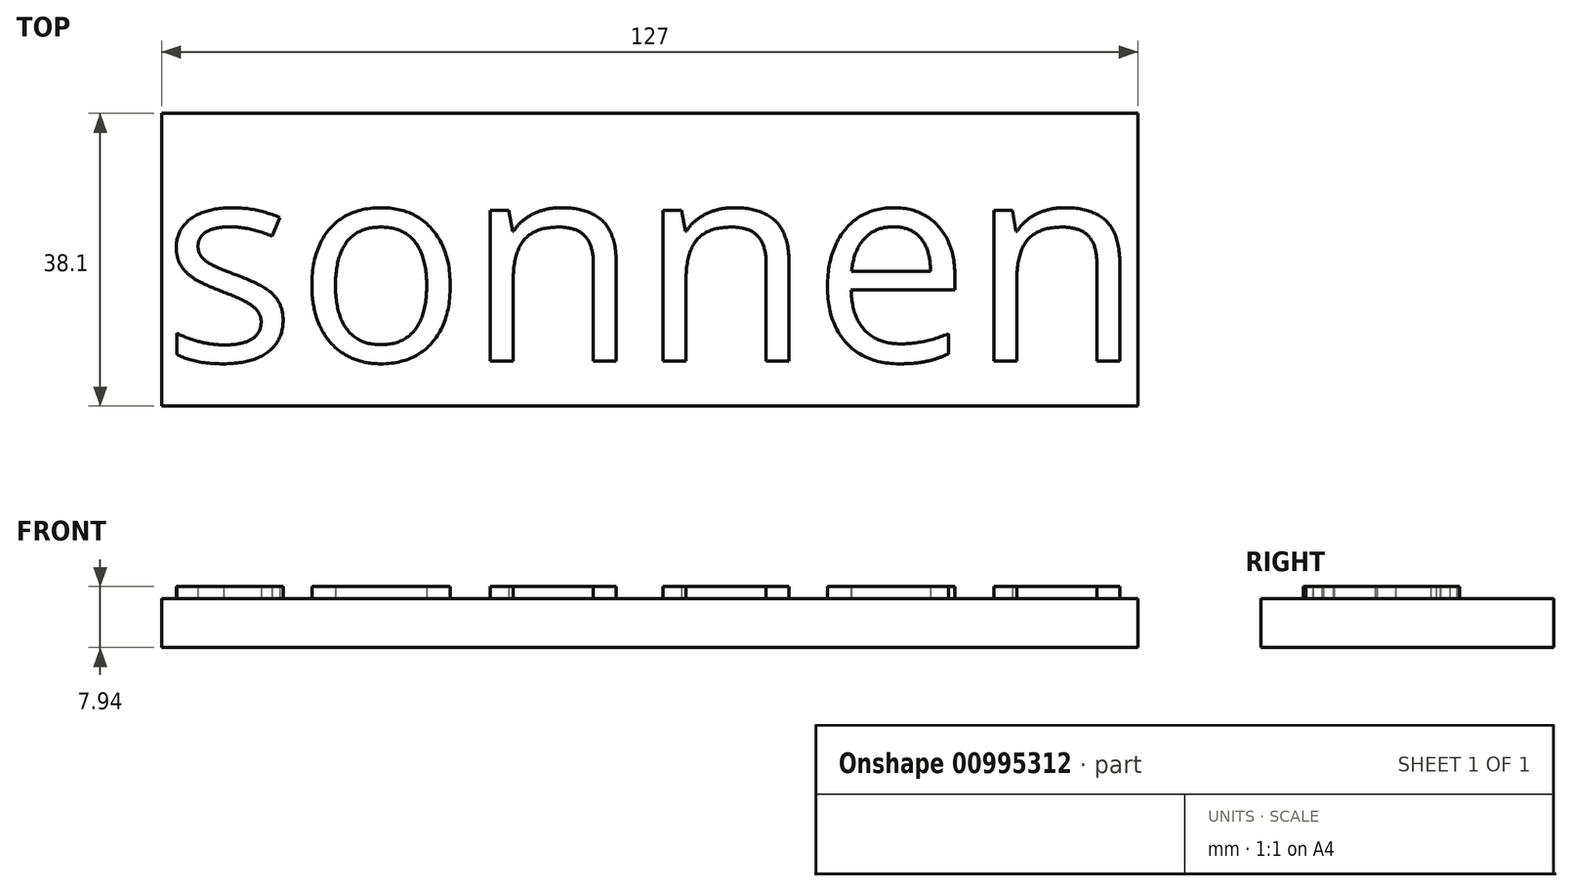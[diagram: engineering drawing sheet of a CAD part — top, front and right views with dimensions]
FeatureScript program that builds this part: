
annotation { "Feature Type Name" : "Feature", "Feature Type Description" : "" }
export const myFeature = defineFeature(function(context is Context, id is Id, definition is map)
    precondition{}
    {
        {
            var Q0;
            Q0=qCreatedBy(makeId("Top.planeOp"),FACE);
            var sketch = newSketch(context, id + "F0", { "sketchPlane" : qUnion([Q0])});
            skLineSegment(sketch, "E0.bottom", {"start": v(-63.5, -19.05) * mm, "end": v(63.5, -19.05) * mm});
            skLineSegment(sketch, "E0.top", {"start": v(-63.5, 19.05) * mm, "end": v(63.5, 19.05) * mm});
            skLineSegment(sketch, "E0.left", {"start": v(-63.5, -19.05) * mm, "end": v(-63.5, 19.05) * mm});
            skLineSegment(sketch, "E0.right", {"start": v(63.5, -19.05) * mm, "end": v(63.5, 19.05) * mm});
            skLineSegment(sketch, "E1", {"start": v(0, 19.05) * mm, "end": v(0, -19.05) * mm, "construction": true});
            skLineSegment(sketch, "E2", {"start": v(-63.5, 0) * mm, "end": v(63.5, 0) * mm, "construction": true});
            skSolve(sketch);
        }
        {
            var Q0;
            Q0 = qSketchRegion(id + "F0", true);
            extrude(context, id + "F1", {"entities" : qUnion([Q0]), "depth" : 6.35 * mm, "offsetDistance" : 25.4 * mm});
        }
        {
            var Q0;
            Q0=makeQuery(id+"F1.opExtrude","CAP_FACE",FACE,{"disambiguationData":[OSD([sQuery(id+"F0.wireOp",EDGE,"E0.bottom"),sQuery(id+"F0.wireOp",EDGE,"E0.top"),sQuery(id+"F0.wireOp",EDGE,"E0.left"),sQuery(id+"F0.wireOp",EDGE,"E0.right")])],"isStart":false});
            var sketch = newSketch(context, id + "F2", { "sketchPlane" : qUnion([Q0])});
            skText(sketch, "E3", { "text": "sonnen", "fontName": "OpenSans-Regular.ttf"});
            const initialGuessF2  = {"E3": [-0.0635, -0.01318, 1, 0, 0.02637]};
            skSetInitialGuess(sketch, initialGuessF2);
            skSolve(sketch);
        }
        {
            var Q0;
            Q0 = qSketchRegion(id + "F2", true);
            extrude(context, id + "F3", {"entities" : qUnion([Q0]), "operationType" : NewBodyOperationType.ADD, "depth" : 1.59 * mm, "offsetDistance" : 25.4 * mm});
        }
    });
